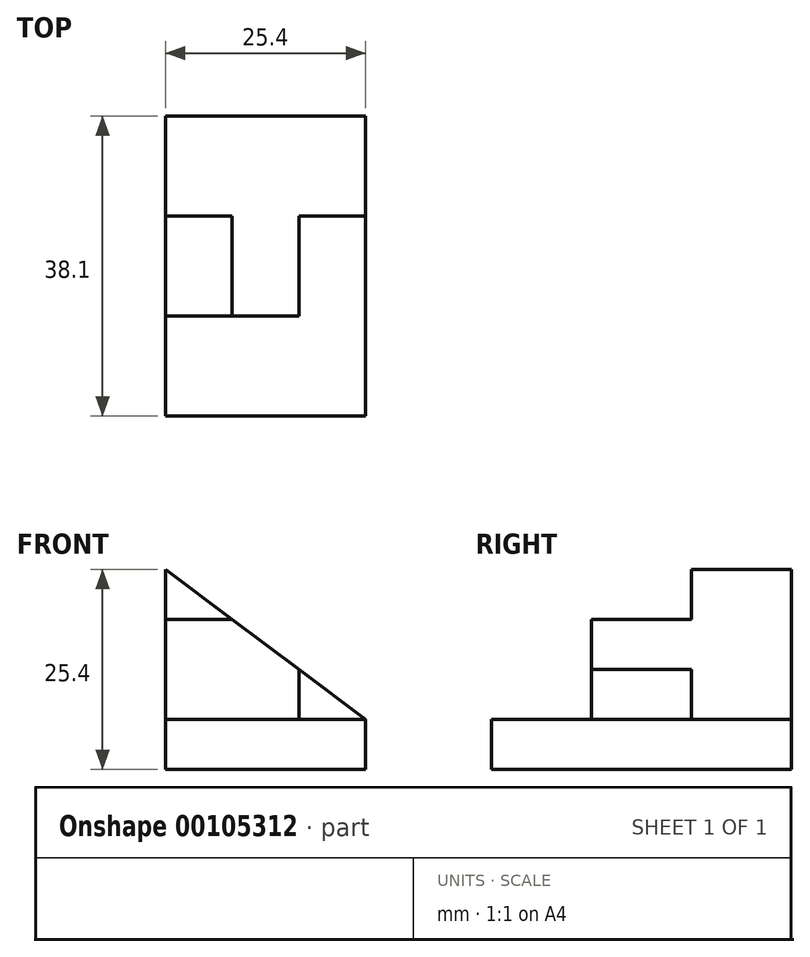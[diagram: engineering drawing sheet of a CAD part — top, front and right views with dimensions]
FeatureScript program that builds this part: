
annotation { "Feature Type Name" : "Feature", "Feature Type Description" : "" }
export const myFeature = defineFeature(function(context is Context, id is Id, definition is map)
    precondition{}
    {
        {
            var Q0;
            Q0=qCreatedBy(makeId("Front.planeOp"),FACE);
            var sketch = newSketch(context, id + "F0", { "sketchPlane" : qUnion([Q0])});
            skLineSegment(sketch, "E0.bottom", {"start": v(0, 0) * mm, "end": v(25.4, 0) * mm});
            skLineSegment(sketch, "E0.top", {"start": v(0, 6.35) * mm, "end": v(25.4, 6.35) * mm});
            skLineSegment(sketch, "E0.left", {"start": v(0, 0) * mm, "end": v(0, 6.35) * mm});
            skLineSegment(sketch, "E0.right", {"start": v(25.4, 0) * mm, "end": v(25.4, 6.35) * mm});
            skLineSegment(sketch, "E1", {"start": v(0, 6.35) * mm, "end": v(0, 25.4) * mm});
            skLineSegment(sketch, "E2", {"start": v(0, 25.4) * mm, "end": v(25.4, 6.35) * mm});
            skLineSegment(sketch, "E3", {"start": v(8.47, 19.05) * mm, "end": v(0, 19.05) * mm});
            skLineSegment(sketch, "E4", {"start": v(16.93, 12.7) * mm, "end": v(16.93, 6.35) * mm});
            skSolve(sketch);
        }
        {
            var Q0;
            Q0=makeQuery(id+"F0.imprint","IMPRINT",FACE,{"disambiguationData":[TD([[makeQuery(id+"F0.imprint","IMPRINT",EDGE,{"derivedFrom":sQuery(id+"F0.wireOp",EDGE,"E0.bottom")}),1.0]])]});
            extrude(context, id + "F1", {"entities" : qUnion([Q0]), "depth" : 38.1 * mm});
        }
        {
            var Q0;
            {var subQ0=sQuery(id+"F0.wireOp",EDGE,"E3");Q0=makeQuery(id+"F0.imprint","IMPRINT",FACE,{"disambiguationData":[TD([[makeQuery(id+"F0.imprint","IMPRINT",EDGE,{"derivedFrom":subQ0}),1.0]])]});}
            extrude(context, id + "F2", {"entities" : qUnion([Q0]), "operationType" : NewBodyOperationType.ADD, "depth" : 25.4 * mm});
        }
        {
            var Q0;
            {var subQ3=sQuery(id+"F0.wireOp",EDGE,"E3");Q0=makeQuery(id+"F0.imprint","IMPRINT",FACE,{"disambiguationData":[TD([[makeQuery(id+"F0.imprint","IMPRINT",EDGE,{"derivedFrom":subQ3}),-1.0]])]});}
            var Q1;
            {var subQ3=sQuery(id+"F0.wireOp",EDGE,"E4");Q1=makeQuery(id+"F0.imprint","IMPRINT",FACE,{"disambiguationData":[TD([[makeQuery(id+"F0.imprint","IMPRINT",EDGE,{"derivedFrom":subQ3}),1.0]])]});}
            extrude(context, id + "F3", {"entities" : qUnion([Q0, Q1]), "operationType" : NewBodyOperationType.ADD, "depth" : 12.7 * mm});
        }
    });
